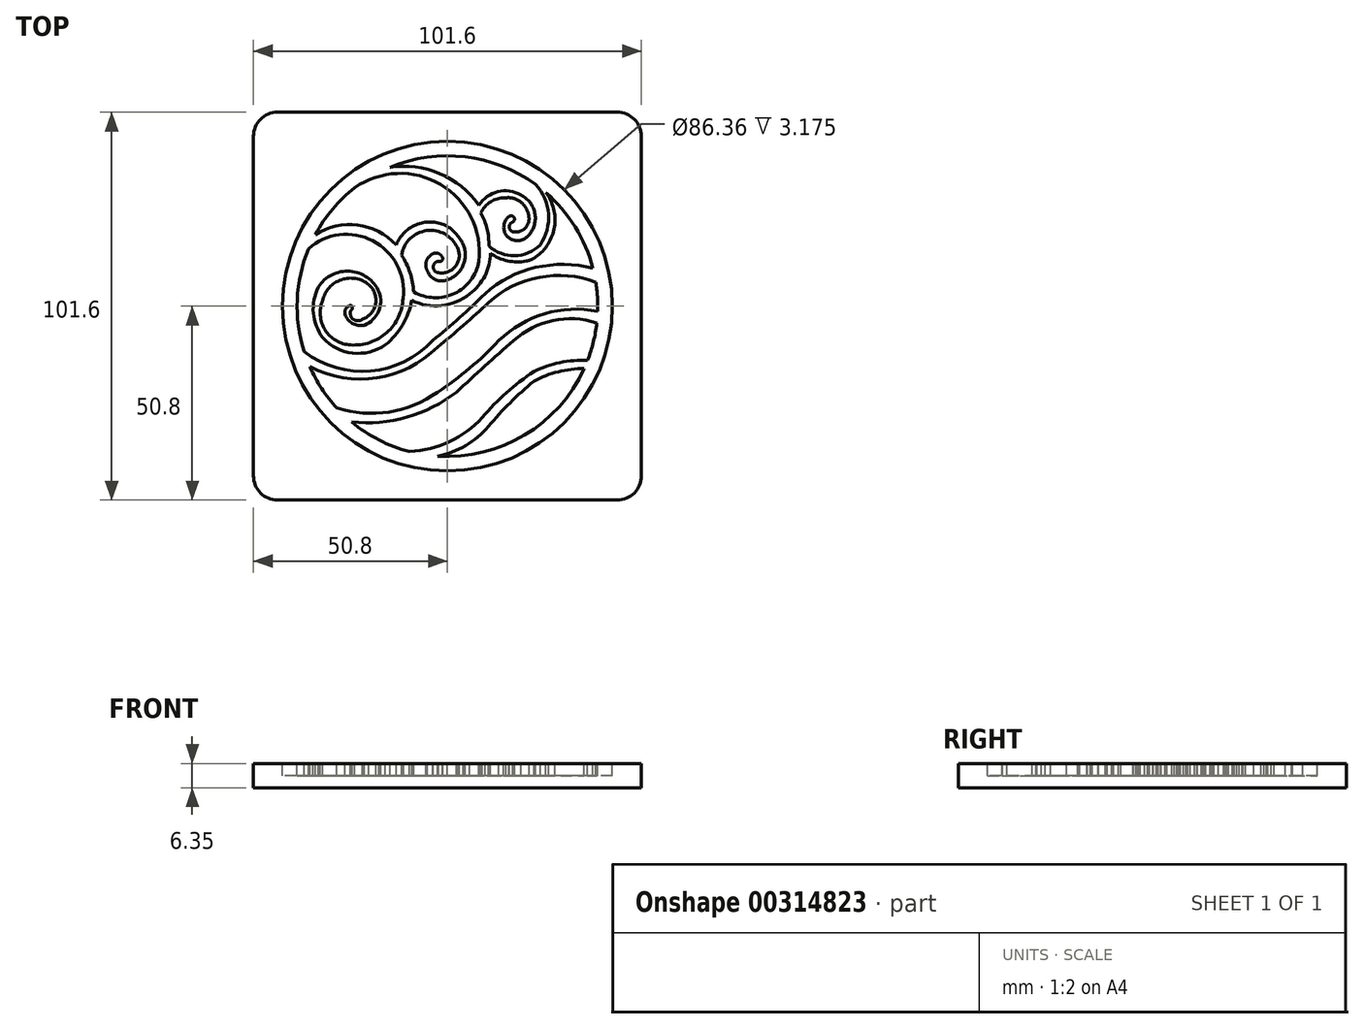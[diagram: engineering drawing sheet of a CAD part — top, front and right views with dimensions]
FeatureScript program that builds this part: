
annotation { "Feature Type Name" : "Feature", "Feature Type Description" : "" }
export const myFeature = defineFeature(function(context is Context, id is Id, definition is map)
    precondition{}
    {
        {
            var Q0;
            Q0=qCreatedBy(makeId("Top.planeOp"),FACE);
            var sketch = newSketch(context, id + "F0", { "sketchPlane" : qUnion([Q0])});
            skLineSegment(sketch, "E0.bottom", {"start": v(-44.45, 50.8) * mm, "end": v(44.45, 50.8) * mm});
            skLineSegment(sketch, "E0.top", {"start": v(-44.45, -50.8) * mm, "end": v(44.45, -50.8) * mm});
            skLineSegment(sketch, "E0.left", {"start": v(-50.8, 44.45) * mm, "end": v(-50.8, -44.45) * mm});
            skLineSegment(sketch, "E0.right", {"start": v(50.8, 44.45) * mm, "end": v(50.8, -44.45) * mm});
            skPoint(sketch, "E1.visualSharp", {"position": v(-50.8, 50.8) * mm});
            skArc(sketch, "E1.filletArc", {"start": v(-44.45, 50.8) * mm, "mid": v(-48.94, 48.94) * mm, "end": v(-50.8, 44.45) * mm});
            skPoint(sketch, "E2.visualSharp", {"position": v(50.8, 50.8) * mm});
            skArc(sketch, "E2.filletArc", {"start": v(50.8, 44.45) * mm, "mid": v(48.94, 48.94) * mm, "end": v(44.45, 50.8) * mm});
            skPoint(sketch, "E3.visualSharp", {"position": v(-50.8, -50.8) * mm});
            skArc(sketch, "E3.filletArc", {"start": v(-50.8, -44.45) * mm, "mid": v(-48.94, -48.94) * mm, "end": v(-44.45, -50.8) * mm});
            skPoint(sketch, "E4.visualSharp", {"position": v(50.8, -50.8) * mm});
            skArc(sketch, "E4.filletArc", {"start": v(44.45, -50.8) * mm, "mid": v(48.94, -48.94) * mm, "end": v(50.8, -44.45) * mm});
            skSolve(sketch);
        }
        {
            var Q0;
            Q0 = qSketchRegion(id + "F0", true);
            extrude(context, id + "F1", {"entities" : qUnion([Q0]), "depth" : 6.35 * mm});
        }
        {
            var Q0;
            Q0=makeQuery(id+"F1.opExtrude","CAP_FACE",FACE,{"disambiguationData":[OSD([sQuery(id+"F0.wireOp",EDGE,"E0.bottom"),sQuery(id+"F0.wireOp",EDGE,"E0.top"),sQuery(id+"F0.wireOp",EDGE,"E0.left"),sQuery(id+"F0.wireOp",EDGE,"E0.right"),sQuery(id+"F0.wireOp",EDGE,"E1.filletArc"),sQuery(id+"F0.wireOp",EDGE,"E2.filletArc"),sQuery(id+"F0.wireOp",EDGE,"E3.filletArc"),sQuery(id+"F0.wireOp",EDGE,"E4.filletArc")])],"isStart":false});
            var sketch = newSketch(context, id + "F2", { "sketchPlane" : qUnion([Q0])});
            skCircle(sketch, "E5", {"center": v(0, 0) * mm, "radius": 43.18 * mm});
            skArc(sketch, "E6", {"start": v(-36.04, -15.86) * mm, "mid": v(-32.94, -21.56) * mm, "end": v(-28.95, -26.68) * mm});
            skArc(sketch, "E7", {"start": v(-36.04, -15.86) * mm, "mid": v(-18.48, -18.78) * mm, "end": v(-2.58, -10.76) * mm});
            skArc(sketch, "E8", {"start": v(-2.58, -10.76) * mm, "mid": v(4.2, -5.02) * mm, "end": v(10.78, 0.96) * mm});
            skArc(sketch, "E9", {"start": v(38.86, 6.3) * mm, "mid": v(24.08, 7.55) * mm, "end": v(10.78, 0.96) * mm});
            skArc(sketch, "E10", {"start": v(-28.95, -26.68) * mm, "mid": v(-15.28, -27.73) * mm, "end": v(-2.58, -22.53) * mm});
            skArc(sketch, "E11", {"start": v(-2.58, -22.53) * mm, "mid": v(5.84, -16.25) * mm, "end": v(13.47, -9.01) * mm});
            skArc(sketch, "E12", {"start": v(39.35, -1.35) * mm, "mid": v(25.46, -1.98) * mm, "end": v(13.47, -9.01) * mm});
            skArc(sketch, "E13", {"start": v(-37.53, -11.88) * mm, "mid": v(-20.1, -16.97) * mm, "end": v(-3.8, -9.01) * mm});
            skArc(sketch, "E14", {"start": v(-3.8, -9.01) * mm, "mid": v(3.18, -3.05) * mm, "end": v(9.82, 3.26) * mm});
            skArc(sketch, "E15", {"start": v(38.11, 9.88) * mm, "mid": v(23.13, 10.13) * mm, "end": v(9.82, 3.26) * mm});
            skArc(sketch, "E16", {"start": v(-25.09, -30.34) * mm, "mid": v(-10.61, -29.1) * mm, "end": v(2.34, -22.53) * mm});
            skArc(sketch, "E17", {"start": v(17.3, -9.01) * mm, "mid": v(9.79, -15.73) * mm, "end": v(2.34, -22.53) * mm});
            skArc(sketch, "E18", {"start": v(39.12, -4.4) * mm, "mid": v(27.6, -3.77) * mm, "end": v(17.3, -9.01) * mm});
            skArc(sketch, "E19", {"start": v(-2.58, -39.29) * mm, "mid": v(4.75, -36.52) * mm, "end": v(10.78, -31.52) * mm});
            skArc(sketch, "E20", {"start": v(22.63, -19.67) * mm, "mid": v(16.43, -25.31) * mm, "end": v(10.78, -31.52) * mm});
            skArc(sketch, "E21", {"start": v(35.83, -16.32) * mm, "mid": v(29.03, -17.2) * mm, "end": v(22.63, -19.67) * mm});
            skArc(sketch, "E22", {"start": v(36.7, -14.23) * mm, "mid": v(29.48, -14.78) * mm, "end": v(22.63, -17.17) * mm});
            skArc(sketch, "E23", {"start": v(22.63, -17.17) * mm, "mid": v(15.46, -22.68) * mm, "end": v(9.17, -29.18) * mm});
            skArc(sketch, "E24", {"start": v(-9.9, -38.1) * mm, "mid": v(0.51, -35.52) * mm, "end": v(9.17, -29.18) * mm});
            skArc(sketch, "E25.trimOffspring", {"start": v(-25.09, -30.34) * mm, "mid": v(-17.92, -35.06) * mm, "end": v(-9.9, -38.1) * mm});
            skArc(sketch, "E26.trimOffspring", {"start": v(-2.58, -39.29) * mm, "mid": v(20.2, -33.8) * mm, "end": v(35.83, -16.32) * mm});
            skArc(sketch, "E27.trimOffspring", {"start": v(36.7, -14.23) * mm, "mid": v(38.23, -9.4) * mm, "end": v(39.12, -4.4) * mm});
            skArc(sketch, "E28.trimOffspring", {"start": v(39.35, -1.35) * mm, "mid": v(39.3, 2.48) * mm, "end": v(38.86, 6.3) * mm});
            skArc(sketch, "E29.trimOffspring", {"start": v(38.11, 9.88) * mm, "mid": v(33.44, 20.79) * mm, "end": v(25.72, 29.8) * mm});
            skArc(sketch, "E30", {"start": v(23.12, 12.84) * mm, "mid": v(28.02, 20.77) * mm, "end": v(25.72, 29.8) * mm});
            skArc(sketch, "E31", {"start": v(11.25, 13.89) * mm, "mid": v(15.75, 11.86) * mm, "end": v(20.69, 11.8) * mm});
            skArc(sketch, "E32", {"start": v(5.81, 3.23) * mm, "mid": v(9.82, 7.9) * mm, "end": v(11.25, 13.89) * mm});
            skArc(sketch, "E33", {"start": v(-9.36, 1.51) * mm, "mid": v(-1.52, 0.16) * mm, "end": v(5.81, 3.23) * mm});
            skArc(sketch, "E34", {"start": v(-16.25, -10.17) * mm, "mid": v(-11.77, -4.94) * mm, "end": v(-9.36, 1.51) * mm});
            skArc(sketch, "E35", {"start": v(-32.67, -8.28) * mm, "mid": v(-24.81, -12.3) * mm, "end": v(-16.25, -10.17) * mm});
            skArc(sketch, "E36", {"start": v(-33.85, 4.96) * mm, "mid": v(-35.1, -1.83) * mm, "end": v(-32.67, -8.28) * mm});
            skArc(sketch, "E37", {"start": v(-17.92, 3.72) * mm, "mid": v(-25.51, 9.13) * mm, "end": v(-33.85, 4.96) * mm});
            skArc(sketch, "E38", {"start": v(-21.8, -5) * mm, "mid": v(-18.06, -1.44) * mm, "end": v(-17.92, 3.72) * mm});
            skArc(sketch, "E39", {"start": v(-26.85, -2.1) * mm, "mid": v(-24.86, -4.49) * mm, "end": v(-21.8, -5) * mm});
            skArc(sketch, "E40", {"start": v(-25.32, 0.24) * mm, "mid": v(-26.55, -0.62) * mm, "end": v(-26.85, -2.1) * mm});
            skArc(sketch, "E41", {"start": v(-25.32, -1.13) * mm, "mid": v(-24.88, -0.44) * mm, "end": v(-25.32, 0.24) * mm});
            skArc(sketch, "E42", {"start": v(-25.32, -1.13) * mm, "mid": v(-24.64, -3.44) * mm, "end": v(-22.22, -3.43) * mm});
            skArc(sketch, "E43", {"start": v(-22.22, -3.43) * mm, "mid": v(-18.81, 0.63) * mm, "end": v(-20.57, 5.63) * mm});
            skArc(sketch, "E44", {"start": v(-20.57, 5.63) * mm, "mid": v(-27.77, 6.94) * mm, "end": v(-32.67, 1.51) * mm});
            skArc(sketch, "E45", {"start": v(-32.67, 1.51) * mm, "mid": v(-32.02, -6.23) * mm, "end": v(-25.32, -10.17) * mm});
            skArc(sketch, "E46", {"start": v(-25.32, -10.17) * mm, "mid": v(-15.87, -6.93) * mm, "end": v(-11.62, 2.1) * mm});
            skArc(sketch, "E47", {"start": v(-11.62, 2.1) * mm, "mid": v(-19.55, 17.12) * mm, "end": v(-36.4, 15.01) * mm});
            skArc(sketch, "E48", {"start": v(-13.44, 16.05) * mm, "mid": v(-23.53, 21.25) * mm, "end": v(-34.61, 18.76) * mm});
            skArc(sketch, "E49", {"start": v(0, 20.9) * mm, "mid": v(-7.8, 21.47) * mm, "end": v(-13.44, 16.05) * mm});
            skArc(sketch, "E50", {"start": v(4.17, 16.05) * mm, "mid": v(2.43, 18.77) * mm, "end": v(0, 20.9) * mm});
            skArc(sketch, "E51", {"start": v(0, 6.86) * mm, "mid": v(4.04, 10.57) * mm, "end": v(4.17, 16.05) * mm});
            skArc(sketch, "E52", {"start": v(-5.2, 9.12) * mm, "mid": v(-3.06, 6.93) * mm, "end": v(0, 6.86) * mm});
            skArc(sketch, "E53", {"start": v(-3.8, 13.72) * mm, "mid": v(-5.54, 11.74) * mm, "end": v(-5.2, 9.12) * mm});
            skArc(sketch, "E54", {"start": v(-1.32, 12.8) * mm, "mid": v(-2.37, 13.79) * mm, "end": v(-3.8, 13.72) * mm});
            skArc(sketch, "E55", {"start": v(-2.27, 11.77) * mm, "mid": v(-1.42, 11.94) * mm, "end": v(-1.32, 12.8) * mm});
            skArc(sketch, "E56", {"start": v(-2.27, 11.77) * mm, "mid": v(-3.7, 10.25) * mm, "end": v(-2.27, 8.73) * mm});
            skArc(sketch, "E57", {"start": v(-2.27, 8.73) * mm, "mid": v(2.2, 10.54) * mm, "end": v(2.6, 15.36) * mm});
            skArc(sketch, "E58", {"start": v(2.6, 15.36) * mm, "mid": v(-5.44, 19.78) * mm, "end": v(-12.02, 13.4) * mm});
            skArc(sketch, "E59", {"start": v(-8.8, 3.72) * mm, "mid": v(-9.81, 8.76) * mm, "end": v(-12.02, 13.4) * mm});
            skArc(sketch, "E60", {"start": v(-8.8, 3.72) * mm, "mid": v(1.82, 3.3) * mm, "end": v(8.26, 11.77) * mm});
            skArc(sketch, "E61", {"start": v(8.26, 11.77) * mm, "mid": v(-1.78, 31.88) * mm, "end": v(-24.25, 31.02) * mm});
            skArc(sketch, "E62", {"start": v(8.26, 26.46) * mm, "mid": v(-2, 34.7) * mm, "end": v(-15.06, 36.37) * mm});
            skArc(sketch, "E63", {"start": v(19.26, 29.09) * mm, "mid": v(13.23, 30) * mm, "end": v(8.26, 26.46) * mm});
            skArc(sketch, "E64", {"start": v(21.37, 18.65) * mm, "mid": v(22.89, 24.4) * mm, "end": v(19.26, 29.09) * mm});
            skArc(sketch, "E65", {"start": v(15.32, 18.65) * mm, "mid": v(18.35, 17.16) * mm, "end": v(21.37, 18.65) * mm});
            skArc(sketch, "E66", {"start": v(16.14, 23.48) * mm, "mid": v(14.8, 21.22) * mm, "end": v(15.32, 18.65) * mm});
            skArc(sketch, "E67", {"start": v(17.15, 22.06) * mm, "mid": v(17.4, 23.3) * mm, "end": v(16.14, 23.48) * mm});
            skArc(sketch, "E68", {"start": v(17.15, 22.06) * mm, "mid": v(16.2, 20.76) * mm, "end": v(17.15, 19.47) * mm});
            skArc(sketch, "E69", {"start": v(17.15, 19.47) * mm, "mid": v(20, 20.13) * mm, "end": v(21.37, 22.72) * mm});
            skArc(sketch, "E70", {"start": v(21.37, 22.72) * mm, "mid": v(19.7, 26.85) * mm, "end": v(15.53, 28.41) * mm});
            skArc(sketch, "E71", {"start": v(15.1, 28.4) * mm, "mid": v(11.34, 27.32) * mm, "end": v(8.76, 24.36) * mm});
            skArc(sketch, "E72", {"start": v(10.83, 15.81) * mm, "mid": v(10.4, 20.23) * mm, "end": v(8.76, 24.36) * mm});
            skArc(sketch, "E73", {"start": v(10.83, 15.81) * mm, "mid": v(17.63, 13.2) * mm, "end": v(24.34, 16.05) * mm});
            skArc(sketch, "E74", {"start": v(24.34, 16.05) * mm, "mid": v(26.45, 24.17) * mm, "end": v(23.1, 31.88) * mm});
            skArc(sketch, "E75.trimOffspring", {"start": v(23.1, 31.88) * mm, "mid": v(4.6, 39.1) * mm, "end": v(-15.06, 36.37) * mm});
            skArc(sketch, "E76.trimOffspring", {"start": v(-24.25, 31.02) * mm, "mid": v(-30.06, 25.42) * mm, "end": v(-34.61, 18.76) * mm});
            skArc(sketch, "E77.trimOffspring", {"start": v(-36.4, 15.01) * mm, "mid": v(-39.33, 1.66) * mm, "end": v(-37.53, -11.88) * mm});
            skPoint(sketch, "E78.visualSharp", {"position": v(21.98, 12.13) * mm});
            skArc(sketch, "E78.filletArc", {"start": v(20.69, 11.8) * mm, "mid": v(21.96, 12.2) * mm, "end": v(23.12, 12.84) * mm});
            skPoint(sketch, "E79.visualSharp", {"position": v(15.32, 28.4) * mm});
            skArc(sketch, "E79.filletArc", {"start": v(15.1, 28.4) * mm, "mid": v(15.32, 28.4) * mm, "end": v(15.53, 28.41) * mm});
            skSolve(sketch);
        }
        {
            var Q0;
            Q0 = qSketchRegion(id + "F2", true);
            extrude(context, id + "F3", {"entities" : qUnion([Q0]), "operationType" : NewBodyOperationType.REMOVE, "oppositeDirection" : true, "depth" : 3.17 * mm});
        }
    });
